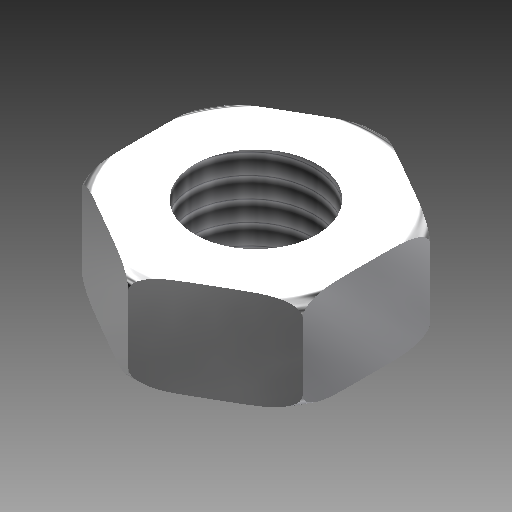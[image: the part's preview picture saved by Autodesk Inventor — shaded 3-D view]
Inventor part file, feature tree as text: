
AUTODESK INVENTOR PART (.ipt)
format: ipt  version: 2018 (Build 220112000, 112)  size: 180,736 bytes
history: native  units: in
note: dims shown in document units (in); Inventor stores cm internally (conversion verified against a paired STEP export)
features: other x3, sketch x2, extrude x1, thread x1, plane x1, revolve x1, mirror x1
ambient origin geometry x8: Origin, YZ Plane, XZ Plane, XY Plane, X Axis, Y Axis, Z Axis, Center Point
bodies: Solid1 (feature_tree)
feature tree (10):
  extrude  "Extrusion1"  Depth=0.095in TaperAngle=0.0deg
  thread  "Thread1"  [1 undecoded]
  sketch  "Sketch3"  dims[d8=0.015in d9=90.0deg]
  other  "Work Point1"
  other  "Work Point2"
  other  "Work Point3"
  plane  "Work Plane1"
  revolve  "Revolution2"  Angle=90.0deg
  mirror  "Mirror1"
  sketch  "Sketch1"  dims[d1=0.1181in d2=0.095in d3=0.0in d4=1.0in d5=0.0in]
note: 1 required parameter value undecoded (feature->parameter linkage not recoverable at this tier; creation-order binding heuristic only, values carry confidence <= 0.55)
